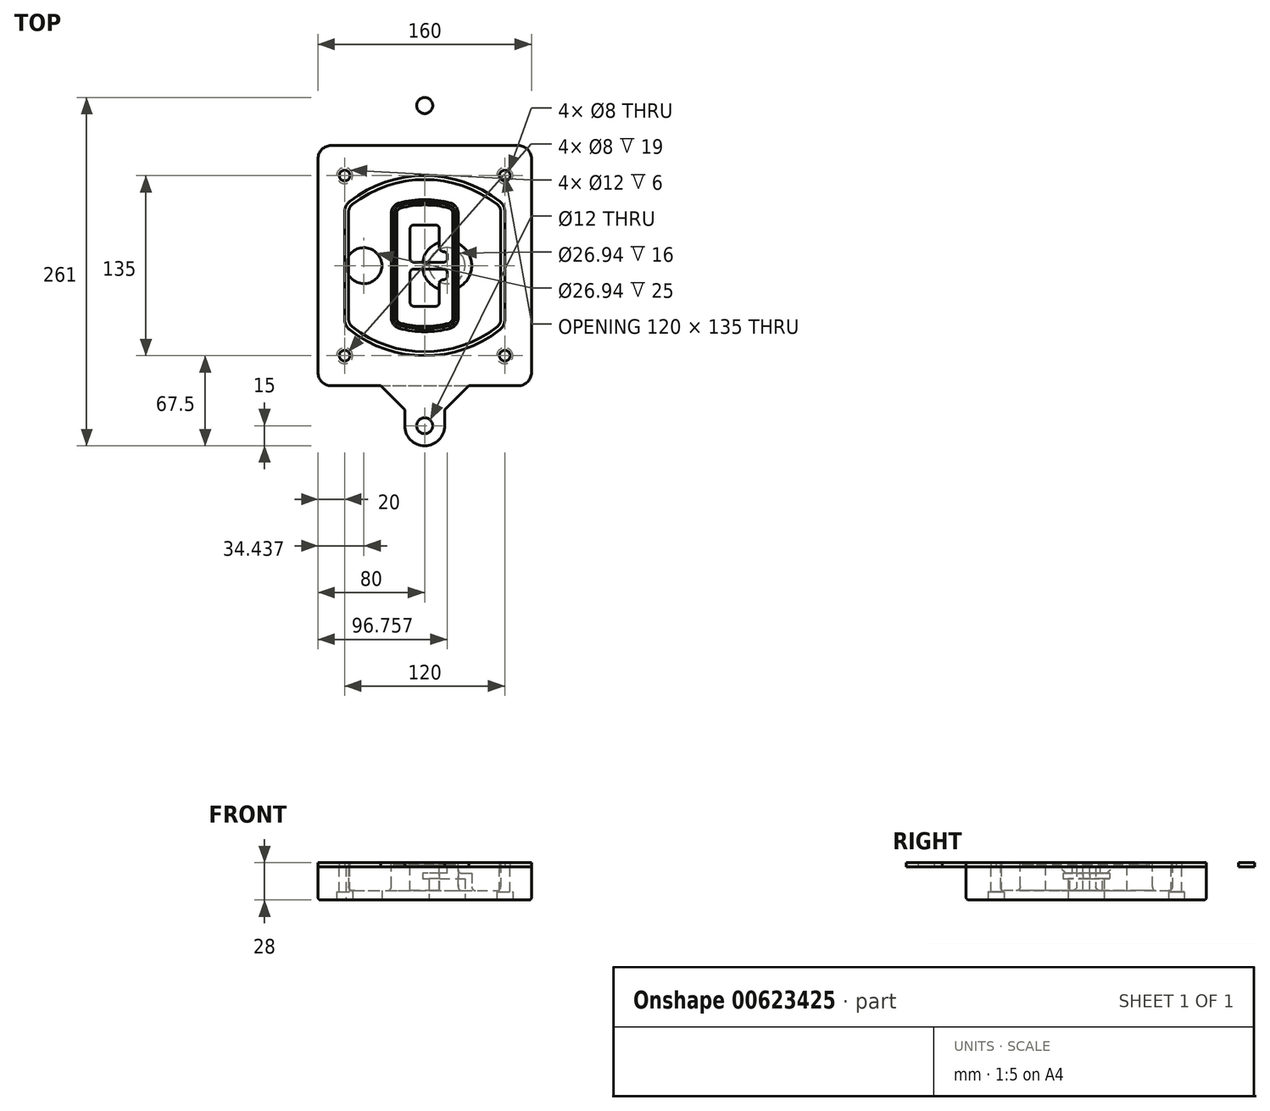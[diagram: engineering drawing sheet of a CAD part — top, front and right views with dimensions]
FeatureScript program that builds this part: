
annotation { "Feature Type Name" : "Feature", "Feature Type Description" : "" }
export const myFeature = defineFeature(function(context is Context, id is Id, definition is map)
    precondition{}
    {
        {
            var Q0;
            Q0=qCreatedBy(makeId("Top.planeOp"),FACE);
            var sketch = newSketch(context, id + "F0", { "sketchPlane" : qUnion([Q0])});
            skPoint(sketch, "E0.rect.middle", {"position": v(0, 0) * mm});
            skLineSegment(sketch, "E1.bottom", {"start": v(-70, -90) * mm, "end": v(70, -90) * mm});
            skLineSegment(sketch, "E1.top", {"start": v(-70, 90) * mm, "end": v(70, 90) * mm});
            skLineSegment(sketch, "E1.left", {"start": v(-80, -80) * mm, "end": v(-80, 80) * mm});
            skLineSegment(sketch, "E1.right", {"start": v(80, -80) * mm, "end": v(80, 80) * mm});
            skLineSegment(sketch, "E2", {"start": v(-80, 90) * mm, "end": v(80, -90) * mm, "construction": true});
            skLineSegment(sketch, "E3", {"start": v(80, 90) * mm, "end": v(-80, -90) * mm, "construction": true});
            skCircle(sketch, "E4", {"center": v(-60, 67.5) * mm, "radius": 4 * mm});
            skCircle(sketch, "E5", {"center": v(60, 67.5) * mm, "radius": 4 * mm});
            skCircle(sketch, "E6", {"center": v(60, -67.5) * mm, "radius": 4 * mm});
            skCircle(sketch, "E7", {"center": v(-60, -67.5) * mm, "radius": 4 * mm});
            skLineSegment(sketch, "E8", {"start": v(-60, 67.5) * mm, "end": v(60, 67.5) * mm, "construction": true});
            skLineSegment(sketch, "E9", {"start": v(60, 67.5) * mm, "end": v(60, -67.5) * mm, "construction": true});
            skLineSegment(sketch, "E10", {"start": v(60, -67.5) * mm, "end": v(-60, -67.5) * mm, "construction": true});
            skLineSegment(sketch, "E11", {"start": v(-60, -67.5) * mm, "end": v(-60, 67.5) * mm, "construction": true});
            skLineSegment(sketch, "E12", {"start": v(-60, 40.3) * mm, "end": v(-60, -40.3) * mm});
            skLineSegment(sketch, "E13", {"start": v(60, 40.3) * mm, "end": v(60, -40.3) * mm});
            skArc(sketch, "E14", {"start": v(56.15, 48.18) * mm, "mid": v(0, 67.5) * mm, "end": v(-56.15, 48.18) * mm});
            skArc(sketch, "E15", {"start": v(-56.15, -48.18) * mm, "mid": v(0, -67.5) * mm, "end": v(56.15, -48.18) * mm});
            skLineSegment(sketch, "E16", {"start": v(-60, 0) * mm, "end": v(60, 0) * mm, "construction": true});
            skPoint(sketch, "E17.visualSharp", {"position": v(-60, -45) * mm});
            skArc(sketch, "E17.filletArc", {"start": v(-60, -40.3) * mm, "mid": v(-58.99, -44.68) * mm, "end": v(-56.15, -48.18) * mm});
            skPoint(sketch, "E18.visualSharp", {"position": v(-60, 45) * mm});
            skArc(sketch, "E18.filletArc", {"start": v(-56.15, 48.18) * mm, "mid": v(-58.99, 44.68) * mm, "end": v(-60, 40.3) * mm});
            skPoint(sketch, "E19.visualSharp", {"position": v(60, 45) * mm});
            skArc(sketch, "E19.filletArc", {"start": v(60, 40.3) * mm, "mid": v(58.99, 44.68) * mm, "end": v(56.15, 48.18) * mm});
            skPoint(sketch, "E20.visualSharp", {"position": v(60, -45) * mm});
            skArc(sketch, "E20.filletArc", {"start": v(56.15, -48.18) * mm, "mid": v(58.99, -44.68) * mm, "end": v(60, -40.3) * mm});
            skPoint(sketch, "E21.visualSharp", {"position": v(-80, 90) * mm});
            skArc(sketch, "E21.filletArc", {"start": v(-70, 90) * mm, "mid": v(-77.07, 87.07) * mm, "end": v(-80, 80) * mm});
            skPoint(sketch, "E22.visualSharp", {"position": v(80, 90) * mm});
            skArc(sketch, "E22.filletArc", {"start": v(80, 80) * mm, "mid": v(77.07, 87.07) * mm, "end": v(70, 90) * mm});
            skPoint(sketch, "E23.visualSharp", {"position": v(80, -90) * mm});
            skArc(sketch, "E23.filletArc", {"start": v(70, -90) * mm, "mid": v(77.07, -87.07) * mm, "end": v(80, -80) * mm});
            skPoint(sketch, "E24.visualSharp", {"position": v(-80, -90) * mm});
            skArc(sketch, "E24.filletArc", {"start": v(-80, -80) * mm, "mid": v(-77.07, -87.07) * mm, "end": v(-70, -90) * mm});
            skArc(sketch, "E25.0", {"start": v(57, 40.3) * mm, "mid": v(56.3, 43.36) * mm, "end": v(54.3, 45.81) * mm});
            skLineSegment(sketch, "E25.1", {"start": v(57, 40.3) * mm, "end": v(57, -40.3) * mm});
            skArc(sketch, "E25.2", {"start": v(54.3, -45.81) * mm, "mid": v(56.3, -43.36) * mm, "end": v(57, -40.3) * mm});
            skArc(sketch, "E25.3", {"start": v(-54.3, -45.81) * mm, "mid": v(0, -64.5) * mm, "end": v(54.3, -45.81) * mm});
            skArc(sketch, "E25.4", {"start": v(-57, -40.3) * mm, "mid": v(-56.3, -43.36) * mm, "end": v(-54.3, -45.81) * mm});
            skArc(sketch, "E25.5", {"start": v(54.3, 45.81) * mm, "mid": v(0, 64.5) * mm, "end": v(-54.3, 45.81) * mm});
            skLineSegment(sketch, "E25.6", {"start": v(-57, 40.3) * mm, "end": v(-57, -40.3) * mm});
            skArc(sketch, "E25.7", {"start": v(-54.3, 45.81) * mm, "mid": v(-56.3, 43.36) * mm, "end": v(-57, 40.3) * mm});
            skArc(sketch, "E26.0", {"start": v(-58.62, 51.33) * mm, "mid": v(-62.58, 46.43) * mm, "end": v(-64, 40.3) * mm});
            skArc(sketch, "E26.1", {"start": v(58.62, 51.33) * mm, "mid": v(0, 71.5) * mm, "end": v(-58.62, 51.33) * mm});
            skArc(sketch, "E26.2", {"start": v(64, 40.3) * mm, "mid": v(62.58, 46.43) * mm, "end": v(58.62, 51.33) * mm});
            skLineSegment(sketch, "E26.3", {"start": v(64, 40.3) * mm, "end": v(64, -40.3) * mm});
            skArc(sketch, "E26.4", {"start": v(58.62, -51.33) * mm, "mid": v(62.58, -46.43) * mm, "end": v(64, -40.3) * mm});
            skLineSegment(sketch, "E26.5", {"start": v(-64, 40.3) * mm, "end": v(-64, -40.3) * mm});
            skArc(sketch, "E26.6", {"start": v(-58.62, -51.33) * mm, "mid": v(0, -71.5) * mm, "end": v(58.62, -51.33) * mm});
            skArc(sketch, "E26.7", {"start": v(-64, -40.3) * mm, "mid": v(-62.58, -46.43) * mm, "end": v(-58.62, -51.33) * mm});
            skSolve(sketch);
        }
        {
            var Q0;
            Q0=makeQuery(id+"F0.imprint","IMPRINT",FACE,{"disambiguationData":[TD([[makeQuery(id+"F0.imprint","IMPRINT",EDGE,{"derivedFrom":sQuery(id+"F0.wireOp",EDGE,"E1.bottom")}),1.0]])]});
            var Q1;
            Q1=makeQuery(id+"F0.imprint","IMPRINT",FACE,{"disambiguationData":[TD([[makeQuery(id+"F0.imprint","IMPRINT",EDGE,{"derivedFrom":sQuery(id+"F0.wireOp",EDGE,"E12")}),1.0]])]});
            var Q2;
            Q2=makeQuery(id+"F0.imprint","IMPRINT",FACE,{"disambiguationData":[TD([[makeQuery(id+"F0.imprint","IMPRINT",EDGE,{"derivedFrom":sQuery(id+"F0.wireOp",EDGE,"E25.0")}),1.0]])]});
            var Q3;
            Q3=makeQuery(id+"F0.imprint","IMPRINT",FACE,{"disambiguationData":[TD([[makeQuery(id+"F0.imprint","IMPRINT",EDGE,{"derivedFrom":sQuery(id+"F0.wireOp",EDGE,"E12")}),-1.0]])]});
            extrude(context, id + "F1", {"entities" : qUnion([Q0, Q1, Q2, Q3]), "oppositeDirection" : true, "depth" : 25 * mm});
        }
        {
            var Q0;
            Q0=makeQuery(id+"F0.imprint","IMPRINT",FACE,{"disambiguationData":[TD([[makeQuery(id+"F0.imprint","IMPRINT",EDGE,{"derivedFrom":sQuery(id+"F0.wireOp",EDGE,"E12")}),1.0]])]});
            extrude(context, id + "F2", {"entities" : qUnion([Q0]), "operationType" : NewBodyOperationType.ADD, "depth" : 3 * mm});
        }
        {
            var Q0;
            Q0=makeQuery(id+"F0.imprint","IMPRINT",FACE,{"disambiguationData":[TD([[makeQuery(id+"F0.imprint","IMPRINT",EDGE,{"derivedFrom":sQuery(id+"F0.wireOp",EDGE,"E25.0")}),1.0]])]});
            extrude(context, id + "F3", {"entities" : qUnion([Q0]), "operationType" : NewBodyOperationType.REMOVE, "oppositeDirection" : true, "depth" : 18 * mm});
        }
        {
            var Q0;
            Q0=makeQuery(id+"F2.opExtrude","CAP_FACE",FACE,{"disambiguationData":[OSD([sQuery(id+"F0.wireOp",EDGE,"E12"),sQuery(id+"F0.wireOp",EDGE,"E13"),sQuery(id+"F0.wireOp",EDGE,"E14"),sQuery(id+"F0.wireOp",EDGE,"E15"),sQuery(id+"F0.wireOp",EDGE,"E17.filletArc"),sQuery(id+"F0.wireOp",EDGE,"E18.filletArc"),sQuery(id+"F0.wireOp",EDGE,"E19.filletArc"),sQuery(id+"F0.wireOp",EDGE,"E20.filletArc"),sQuery(id+"F0.wireOp",EDGE,"E25.0"),sQuery(id+"F0.wireOp",EDGE,"E25.1"),sQuery(id+"F0.wireOp",EDGE,"E25.2"),sQuery(id+"F0.wireOp",EDGE,"E25.3"),sQuery(id+"F0.wireOp",EDGE,"E25.4"),sQuery(id+"F0.wireOp",EDGE,"E25.5"),sQuery(id+"F0.wireOp",EDGE,"E25.6"),sQuery(id+"F0.wireOp",EDGE,"E25.7")])],"isStart":false});
            var sketch = newSketch(context, id + "F4", { "sketchPlane" : qUnion([Q0])});
            skArc(sketch, "E27.0", {"start": v(-19.08, -46.97) * mm, "mid": v(0, -49.5) * mm, "end": v(19.08, -46.97) * mm});
            skArc(sketch, "E28.0", {"start": v(19.08, 46.97) * mm, "mid": v(0, 49.5) * mm, "end": v(-19.08, 46.97) * mm});
            skLineSegment(sketch, "E29", {"start": v(-25, 39.25) * mm, "end": v(-25, -39.25) * mm});
            skLineSegment(sketch, "E30", {"start": v(25, 39.25) * mm, "end": v(25, -39.25) * mm});
            skLineSegment(sketch, "E31", {"start": v(-25, 45.1) * mm, "end": v(25, 45.1) * mm, "construction": true});
            skLineSegment(sketch, "E32", {"start": v(-25, -45.1) * mm, "end": v(25, -45.1) * mm, "construction": true});
            skPoint(sketch, "E33.visualSharp", {"position": v(-25, 45.1) * mm});
            skArc(sketch, "E33.filletArc", {"start": v(-19.08, 46.97) * mm, "mid": v(-23.35, 44.11) * mm, "end": v(-25, 39.25) * mm});
            skPoint(sketch, "E34.visualSharp", {"position": v(25, 45.1) * mm});
            skArc(sketch, "E34.filletArc", {"start": v(25, 39.25) * mm, "mid": v(23.35, 44.11) * mm, "end": v(19.08, 46.97) * mm});
            skPoint(sketch, "E35.visualSharp", {"position": v(25, -45.1) * mm});
            skArc(sketch, "E35.filletArc", {"start": v(19.08, -46.97) * mm, "mid": v(23.35, -44.11) * mm, "end": v(25, -39.25) * mm});
            skPoint(sketch, "E36.visualSharp", {"position": v(-25, -45.1) * mm});
            skArc(sketch, "E36.filletArc", {"start": v(-25, -39.25) * mm, "mid": v(-23.35, -44.11) * mm, "end": v(-19.08, -46.97) * mm});
            skArc(sketch, "E37.0", {"start": v(54.3, 45.81) * mm, "mid": v(0, 64.5) * mm, "end": v(-54.3, 45.81) * mm});
            skArc(sketch, "E37.1", {"start": v(-54.3, 45.81) * mm, "mid": v(-56.3, 43.36) * mm, "end": v(-57, 40.3) * mm});
            skLineSegment(sketch, "E37.2", {"start": v(-57, 40.3) * mm, "end": v(-57, -40.3) * mm});
            skArc(sketch, "E37.3", {"start": v(-57, -40.3) * mm, "mid": v(-56.3, -43.36) * mm, "end": v(-54.3, -45.81) * mm});
            skArc(sketch, "E37.4", {"start": v(-54.3, -45.81) * mm, "mid": v(0, -64.5) * mm, "end": v(54.3, -45.81) * mm});
            skArc(sketch, "E37.5", {"start": v(54.3, -45.81) * mm, "mid": v(56.3, -43.36) * mm, "end": v(57, -40.3) * mm});
            skLineSegment(sketch, "E37.6", {"start": v(57, 40.3) * mm, "end": v(57, -40.3) * mm});
            skArc(sketch, "E37.7", {"start": v(57, 40.3) * mm, "mid": v(56.3, 43.36) * mm, "end": v(54.3, 45.81) * mm});
            skLineSegment(sketch, "E38.0", {"start": v(23, 39.25) * mm, "end": v(23, -39.25) * mm});
            skArc(sketch, "E38.1", {"start": v(18.56, -45.04) * mm, "mid": v(21.76, -42.9) * mm, "end": v(23, -39.25) * mm});
            skArc(sketch, "E38.2", {"start": v(-18.56, -45.04) * mm, "mid": v(0, -47.5) * mm, "end": v(18.56, -45.04) * mm});
            skArc(sketch, "E38.3", {"start": v(-23, -39.25) * mm, "mid": v(-21.76, -42.9) * mm, "end": v(-18.56, -45.04) * mm});
            skLineSegment(sketch, "E38.4", {"start": v(-23, 39.25) * mm, "end": v(-23, -39.25) * mm});
            skArc(sketch, "E38.5", {"start": v(23, 39.25) * mm, "mid": v(21.76, 42.9) * mm, "end": v(18.56, 45.04) * mm});
            skArc(sketch, "E38.6", {"start": v(-18.56, 45.04) * mm, "mid": v(-21.76, 42.9) * mm, "end": v(-23, 39.25) * mm});
            skArc(sketch, "E38.7", {"start": v(18.56, 45.04) * mm, "mid": v(0, 47.5) * mm, "end": v(-18.56, 45.04) * mm});
            skArc(sketch, "E39.0", {"start": v(21, 39.25) * mm, "mid": v(20.18, 41.68) * mm, "end": v(18.04, 43.1) * mm});
            skLineSegment(sketch, "E39.1", {"start": v(21, 39.25) * mm, "end": v(21, -39.25) * mm});
            skArc(sketch, "E39.2", {"start": v(18.04, -43.1) * mm, "mid": v(20.18, -41.68) * mm, "end": v(21, -39.25) * mm});
            skArc(sketch, "E39.3", {"start": v(-18.04, -43.1) * mm, "mid": v(0, -45.5) * mm, "end": v(18.04, -43.1) * mm});
            skArc(sketch, "E39.4", {"start": v(-21, -39.25) * mm, "mid": v(-20.18, -41.68) * mm, "end": v(-18.04, -43.1) * mm});
            skArc(sketch, "E39.5", {"start": v(18.04, 43.1) * mm, "mid": v(0, 45.5) * mm, "end": v(-18.04, 43.1) * mm});
            skLineSegment(sketch, "E39.6", {"start": v(-21, 39.25) * mm, "end": v(-21, -39.25) * mm});
            skArc(sketch, "E39.7", {"start": v(-18.04, 43.1) * mm, "mid": v(-20.18, 41.68) * mm, "end": v(-21, 39.25) * mm});
            skLineSegment(sketch, "E40", {"start": v(-25, 0) * mm, "end": v(25, 0) * mm, "construction": true});
            skLineSegment(sketch, "E41", {"start": v(-11, 5.5) * mm, "end": v(-11, 27.5) * mm});
            skLineSegment(sketch, "E42", {"start": v(-8, 30.5) * mm, "end": v(8, 30.5) * mm});
            skLineSegment(sketch, "E43", {"start": v(11, 27.5) * mm, "end": v(11, 13.5) * mm});
            skLineSegment(sketch, "E44", {"start": v(14, 10.5) * mm, "end": v(14, 10.5) * mm});
            skLineSegment(sketch, "E45", {"start": v(17, 7.5) * mm, "end": v(17, 5.5) * mm});
            skLineSegment(sketch, "E46", {"start": v(14, 2.5) * mm, "end": v(-8, 2.5) * mm});
            skPoint(sketch, "E47.visualSharp", {"position": v(-11, 30.5) * mm});
            skArc(sketch, "E47.filletArc", {"start": v(-8, 30.5) * mm, "mid": v(-10.12, 29.62) * mm, "end": v(-11, 27.5) * mm});
            skPoint(sketch, "E48.visualSharp", {"position": v(11, 30.5) * mm});
            skArc(sketch, "E48.filletArc", {"start": v(11, 27.5) * mm, "mid": v(10.12, 29.62) * mm, "end": v(8, 30.5) * mm});
            skPoint(sketch, "E49.visualSharp", {"position": v(11, 10.5) * mm});
            skArc(sketch, "E49.filletArc", {"start": v(11, 13.5) * mm, "mid": v(11.88, 11.38) * mm, "end": v(14, 10.5) * mm});
            skPoint(sketch, "E50.visualSharp", {"position": v(17, 10.5) * mm});
            skArc(sketch, "E50.filletArc", {"start": v(17, 7.5) * mm, "mid": v(16.12, 9.62) * mm, "end": v(14, 10.5) * mm});
            skPoint(sketch, "E51.visualSharp", {"position": v(17, 2.5) * mm});
            skArc(sketch, "E51.filletArc", {"start": v(14, 2.5) * mm, "mid": v(16.12, 3.38) * mm, "end": v(17, 5.5) * mm});
            skPoint(sketch, "E52.visualSharp", {"position": v(-11, 2.5) * mm});
            skArc(sketch, "E52.filletArc", {"start": v(-11, 5.5) * mm, "mid": v(-10.12, 3.38) * mm, "end": v(-8, 2.5) * mm});
            skLineSegment(sketch, "E53.0.MirrorCS", {"start": v(14, -2.5) * mm, "end": v(-8, -2.5) * mm});
            skArc(sketch, "E54.0.MirrorCS", {"start": v(-11, -5.5) * mm, "mid": v(-10.12, -3.38) * mm, "end": v(-8, -2.5) * mm});
            skLineSegment(sketch, "E55.0.MirrorCS", {"start": v(-11, -5.5) * mm, "end": v(-11, -27.5) * mm});
            skArc(sketch, "E56.0.MirrorCS", {"start": v(-8, -30.5) * mm, "mid": v(-10.12, -29.62) * mm, "end": v(-11, -27.5) * mm});
            skLineSegment(sketch, "E57.0.MirrorCS", {"start": v(-8, -30.5) * mm, "end": v(8, -30.5) * mm});
            skArc(sketch, "E58.0.MirrorCS", {"start": v(11, -27.5) * mm, "mid": v(10.12, -29.62) * mm, "end": v(8, -30.5) * mm});
            skLineSegment(sketch, "E59.0.MirrorCS", {"start": v(11, -27.5) * mm, "end": v(11, -13.5) * mm});
            skArc(sketch, "E60.0.MirrorCS", {"start": v(11, -13.5) * mm, "mid": v(11.88, -11.38) * mm, "end": v(14, -10.5) * mm});
            skArc(sketch, "E61.0.MirrorCS", {"start": v(17, -7.5) * mm, "mid": v(16.12, -9.62) * mm, "end": v(14, -10.5) * mm});
            skLineSegment(sketch, "E62.0.MirrorCS", {"start": v(17, -7.5) * mm, "end": v(17, -5.5) * mm});
            skArc(sketch, "E63.0.MirrorCS", {"start": v(14, -2.5) * mm, "mid": v(16.12, -3.38) * mm, "end": v(17, -5.5) * mm});
            skSolve(sketch);
        }
        {
            var Q0;
            Q0=makeQuery(id+"F4.imprint","IMPRINT",FACE,{"disambiguationData":[TD([[makeQuery(id+"F4.imprint","IMPRINT",EDGE,{"derivedFrom":sQuery(id+"F4.wireOp",EDGE,"E27.0")}),1.0]])]});
            var Q1;
            Q1=makeQuery(id+"F4.imprint","IMPRINT",FACE,{"disambiguationData":[TD([[makeQuery(id+"F4.imprint","IMPRINT",EDGE,{"derivedFrom":sQuery(id+"F4.wireOp",EDGE,"E38.0")}),-1.0]])]});
            var Q2;
            Q2=makeQuery(id+"F4.imprint","IMPRINT",FACE,{"disambiguationData":[TD([[makeQuery(id+"F4.imprint","IMPRINT",EDGE,{"derivedFrom":sQuery(id+"F4.wireOp",EDGE,"E39.0")}),1.0]])]});
            extrude(context, id + "F5", {"entities" : qUnion([Q0, Q1, Q2]), "operationType" : NewBodyOperationType.ADD, "endBound" : BoundingType.UP_TO_NEXT, "oppositeDirection" : true, "depth" : 25 * mm});
        }
        {
            var Q0;
            Q0=makeQuery(id+"F4.imprint","IMPRINT",FACE,{"disambiguationData":[TD([[makeQuery(id+"F4.imprint","IMPRINT",EDGE,{"derivedFrom":sQuery(id+"F4.wireOp",EDGE,"E38.0")}),-1.0]])]});
            extrude(context, id + "F6", {"entities" : qUnion([Q0]), "operationType" : NewBodyOperationType.REMOVE, "oppositeDirection" : true, "depth" : 2 * mm});
        }
        {
            var Q0;
            Q0=makeQuery(id+"F1.opExtrude","CAP_FACE",FACE,{"disambiguationData":[OSD([sQuery(id+"F0.wireOp",EDGE,"E1.bottom"),sQuery(id+"F0.wireOp",EDGE,"E1.top"),sQuery(id+"F0.wireOp",EDGE,"E1.left"),sQuery(id+"F0.wireOp",EDGE,"E1.right"),sQuery(id+"F0.wireOp",EDGE,"E4"),sQuery(id+"F0.wireOp",EDGE,"E5"),sQuery(id+"F0.wireOp",EDGE,"E6"),sQuery(id+"F0.wireOp",EDGE,"E7"),sQuery(id+"F0.wireOp",EDGE,"E21.filletArc"),sQuery(id+"F0.wireOp",EDGE,"E22.filletArc"),sQuery(id+"F0.wireOp",EDGE,"E23.filletArc"),sQuery(id+"F0.wireOp",EDGE,"E24.filletArc")])],"isStart":false});
            var sketch = newSketch(context, id + "F7", { "sketchPlane" : qUnion([Q0])});
            skCircle(sketch, "E64", {"center": v(16.76, 0) * mm, "radius": 13.47 * mm});
            skCircle(sketch, "E65", {"center": v(-45.56, 0) * mm, "radius": 13.47 * mm});
            skLineSegment(sketch, "E66", {"start": v(80, 0) * mm, "end": v(-80, 0) * mm});
            skCircle(sketch, "E67", {"center": v(16.76, 0) * mm, "radius": 18.47 * mm});
            skCircle(sketch, "E68", {"center": v(60, -67.5) * mm, "radius": 6 * mm});
            skCircle(sketch, "E69", {"center": v(-60, -67.5) * mm, "radius": 6 * mm});
            skCircle(sketch, "E70", {"center": v(-60, 67.5) * mm, "radius": 6 * mm});
            skCircle(sketch, "E71", {"center": v(60, 67.5) * mm, "radius": 6 * mm});
            skSolve(sketch);
        }
        {
            var Q0;
            {var subQ1=sQuery(id+"F7.wireOp",EDGE,"E66");var subQ4=sQuery(id+"F7.wireOp",EDGE,"E64");var subQ6=makeQuery(id+"F7.imprint","INTERSECT",VERTEX,{"disambiguationData":[OD(0.0)],"derivedFrom":[subQ4,subQ1]});Q0=makeQuery(id+"F7.imprint","IMPRINT",FACE,{"disambiguationData":[TD([[makeQuery(id+"F7.imprint","IMPRINT",EDGE,{"disambiguationData":[TD([[subQ6,-1.0]])],"derivedFrom":subQ4}),-1.0]])]});}
            var Q1;
            {var subQ0=sQuery(id+"F7.wireOp",EDGE,"E66");var subQ1=sQuery(id+"F7.wireOp",EDGE,"E64");var subQ3=makeQuery(id+"F7.imprint","INTERSECT",VERTEX,{"disambiguationData":[OD(0.0)],"derivedFrom":[subQ1,subQ0]});Q1=makeQuery(id+"F7.imprint","IMPRINT",FACE,{"disambiguationData":[TD([[makeQuery(id+"F7.imprint","IMPRINT",EDGE,{"disambiguationData":[TD([[subQ3,-1.0]])],"derivedFrom":subQ1}),1.0]])]});}
            var Q2;
            {var subQ0=sQuery(id+"F7.wireOp",EDGE,"E66");var subQ1=sQuery(id+"F7.wireOp",EDGE,"E64");var subQ3=makeQuery(id+"F7.imprint","INTERSECT",VERTEX,{"disambiguationData":[OD(0.0)],"derivedFrom":[subQ1,subQ0]});Q2=makeQuery(id+"F7.imprint","IMPRINT",FACE,{"disambiguationData":[TD([[makeQuery(id+"F7.imprint","IMPRINT",EDGE,{"disambiguationData":[TD([[subQ3,1.0]])],"derivedFrom":subQ1}),1.0]])]});}
            var Q3;
            {var subQ1=sQuery(id+"F7.wireOp",EDGE,"E66");var subQ4=sQuery(id+"F7.wireOp",EDGE,"E64");var subQ6=makeQuery(id+"F7.imprint","INTERSECT",VERTEX,{"disambiguationData":[OD(0.0)],"derivedFrom":[subQ4,subQ1]});Q3=makeQuery(id+"F7.imprint","IMPRINT",FACE,{"disambiguationData":[TD([[makeQuery(id+"F7.imprint","IMPRINT",EDGE,{"disambiguationData":[TD([[subQ6,1.0]])],"derivedFrom":subQ4}),-1.0]])]});}
            extrude(context, id + "F8", {"entities" : qUnion([Q0, Q1, Q2, Q3]), "operationType" : NewBodyOperationType.ADD, "oppositeDirection" : true, "depth" : 20 * mm});
        }
        {
            var Q0;
            {var subQ0=sQuery(id+"F7.wireOp",EDGE,"E66");var subQ1=sQuery(id+"F7.wireOp",EDGE,"E64");var subQ3=makeQuery(id+"F7.imprint","INTERSECT",VERTEX,{"disambiguationData":[OD(0.0)],"derivedFrom":[subQ1,subQ0]});Q0=makeQuery(id+"F7.imprint","IMPRINT",FACE,{"disambiguationData":[TD([[makeQuery(id+"F7.imprint","IMPRINT",EDGE,{"disambiguationData":[TD([[subQ3,-1.0]])],"derivedFrom":subQ1}),1.0]])]});}
            var Q1;
            {var subQ0=sQuery(id+"F7.wireOp",EDGE,"E66");var subQ1=sQuery(id+"F7.wireOp",EDGE,"E64");var subQ3=makeQuery(id+"F7.imprint","INTERSECT",VERTEX,{"disambiguationData":[OD(0.0)],"derivedFrom":[subQ1,subQ0]});Q1=makeQuery(id+"F7.imprint","IMPRINT",FACE,{"disambiguationData":[TD([[makeQuery(id+"F7.imprint","IMPRINT",EDGE,{"disambiguationData":[TD([[subQ3,1.0]])],"derivedFrom":subQ1}),1.0]])]});}
            extrude(context, id + "F9", {"entities" : qUnion([Q0, Q1]), "operationType" : NewBodyOperationType.REMOVE, "oppositeDirection" : true, "depth" : 16 * mm});
        }
        {
            var Q0;
            {var subQ0=sQuery(id+"F7.wireOp",EDGE,"E66");var subQ1=sQuery(id+"F7.wireOp",EDGE,"E65");var subQ3=makeQuery(id+"F7.imprint","INTERSECT",VERTEX,{"disambiguationData":[OD(0.0)],"derivedFrom":[subQ1,subQ0]});Q0=makeQuery(id+"F7.imprint","IMPRINT",FACE,{"disambiguationData":[TD([[makeQuery(id+"F7.imprint","IMPRINT",EDGE,{"disambiguationData":[TD([[subQ3,-1.0]])],"derivedFrom":subQ1}),1.0]])]});}
            var Q1;
            {var subQ0=sQuery(id+"F7.wireOp",EDGE,"E66");var subQ1=sQuery(id+"F7.wireOp",EDGE,"E65");var subQ3=makeQuery(id+"F7.imprint","INTERSECT",VERTEX,{"disambiguationData":[OD(0.0)],"derivedFrom":[subQ1,subQ0]});Q1=makeQuery(id+"F7.imprint","IMPRINT",FACE,{"disambiguationData":[TD([[makeQuery(id+"F7.imprint","IMPRINT",EDGE,{"disambiguationData":[TD([[subQ3,1.0]])],"derivedFrom":subQ1}),1.0]])]});}
            extrude(context, id + "F10", {"entities" : qUnion([Q0, Q1]), "operationType" : NewBodyOperationType.REMOVE, "oppositeDirection" : true, "depth" : 25 * mm});
        }
        {
            var Q0;
            Q0=makeQuery(id+"F7.imprint","IMPRINT",FACE,{"disambiguationData":[TD([[makeQuery(id+"F7.imprint","IMPRINT",EDGE,{"derivedFrom":sQuery(id+"F7.wireOp",EDGE,"E68")}),1.0]])]});
            var Q1;
            Q1=makeQuery(id+"F7.imprint","IMPRINT",FACE,{"disambiguationData":[TD([[makeQuery(id+"F7.imprint","IMPRINT",EDGE,{"derivedFrom":makeQuery(id+"F1.opExtrude","CAP_EDGE",EDGE,{"disambiguationData":[OSD([sQuery(id+"F0.wireOp",EDGE,"E5")])],"isStart":false})}),-1.0]])]});
            var Q2;
            Q2=makeQuery(id+"F7.imprint","IMPRINT",FACE,{"disambiguationData":[TD([[makeQuery(id+"F7.imprint","IMPRINT",EDGE,{"derivedFrom":sQuery(id+"F7.wireOp",EDGE,"E69")}),1.0]])]});
            var Q3;
            Q3=makeQuery(id+"F7.imprint","IMPRINT",FACE,{"disambiguationData":[TD([[makeQuery(id+"F7.imprint","IMPRINT",EDGE,{"derivedFrom":makeQuery(id+"F1.opExtrude","CAP_EDGE",EDGE,{"disambiguationData":[OSD([sQuery(id+"F0.wireOp",EDGE,"E4")])],"isStart":false})}),-1.0]])]});
            var Q4;
            Q4=makeQuery(id+"F7.imprint","IMPRINT",FACE,{"disambiguationData":[TD([[makeQuery(id+"F7.imprint","IMPRINT",EDGE,{"derivedFrom":sQuery(id+"F7.wireOp",EDGE,"E70")}),1.0]])]});
            var Q5;
            Q5=makeQuery(id+"F7.imprint","IMPRINT",FACE,{"disambiguationData":[TD([[makeQuery(id+"F7.imprint","IMPRINT",EDGE,{"derivedFrom":makeQuery(id+"F1.opExtrude","CAP_EDGE",EDGE,{"disambiguationData":[OSD([sQuery(id+"F0.wireOp",EDGE,"E7")])],"isStart":false})}),-1.0]])]});
            var Q6;
            Q6=makeQuery(id+"F7.imprint","IMPRINT",FACE,{"disambiguationData":[TD([[makeQuery(id+"F7.imprint","IMPRINT",EDGE,{"derivedFrom":sQuery(id+"F7.wireOp",EDGE,"E71")}),1.0]])]});
            var Q7;
            Q7=makeQuery(id+"F7.imprint","IMPRINT",FACE,{"disambiguationData":[TD([[makeQuery(id+"F7.imprint","IMPRINT",EDGE,{"derivedFrom":makeQuery(id+"F1.opExtrude","CAP_EDGE",EDGE,{"disambiguationData":[OSD([sQuery(id+"F0.wireOp",EDGE,"E6")])],"isStart":false})}),-1.0]])]});
            extrude(context, id + "F11", {"entities" : qUnion([Q0, Q1, Q2, Q3, Q4, Q5, Q6, Q7]), "operationType" : NewBodyOperationType.REMOVE, "oppositeDirection" : true, "depth" : 6 * mm});
        }
        {
            var Q0;
            Q0=makeQuery(id+"F9.boolean.opBoolean","COPY",FACE,{"derivedFrom":makeQuery(id+"F9.opExtrude","CAP_FACE",FACE,{"disambiguationData":[OSD([sQuery(id+"F7.wireOp",EDGE,"E64")])],"isStart":false})});
            var sketch = newSketch(context, id + "F12", { "sketchPlane" : qUnion([Q0])});
            skArc(sketch, "E72.0", {"start": v(11, 17.55) * mm, "mid": v(2.57, 11.82) * mm, "end": v(-1.54, 2.5) * mm});
            skArc(sketch, "E72.1", {"start": v(-1.54, -2.5) * mm, "mid": v(2.57, -11.82) * mm, "end": v(11, -17.55) * mm});
            skLineSegment(sketch, "E73", {"start": v(-1.54, -2.5) * mm, "end": v(14, -2.5) * mm});
            skLineSegment(sketch, "E74.0", {"start": v(14, 2.5) * mm, "end": v(-1.54, 2.5) * mm});
            skArc(sketch, "E74.1", {"start": v(14, 2.5) * mm, "mid": v(16.12, 3.38) * mm, "end": v(17, 5.5) * mm});
            skLineSegment(sketch, "E74.2", {"start": v(17, 7.5) * mm, "end": v(17, 5.5) * mm});
            skArc(sketch, "E74.3", {"start": v(17, 7.5) * mm, "mid": v(16.12, 9.62) * mm, "end": v(14, 10.5) * mm});
            skArc(sketch, "E74.4", {"start": v(11, 13.5) * mm, "mid": v(11.88, 11.38) * mm, "end": v(14, 10.5) * mm});
            skLineSegment(sketch, "E74.5", {"start": v(11, 17.55) * mm, "end": v(11, 13.5) * mm});
            skLineSegment(sketch, "E74.7", {"start": v(14, -2.5) * mm, "end": v(-1.54, -2.5) * mm});
            skArc(sketch, "E74.8", {"start": v(14, -2.5) * mm, "mid": v(16.12, -3.38) * mm, "end": v(17, -5.5) * mm});
            skLineSegment(sketch, "E74.9", {"start": v(17, -7.5) * mm, "end": v(17, -5.5) * mm});
            skArc(sketch, "E74.10", {"start": v(17, -7.5) * mm, "mid": v(16.12, -9.62) * mm, "end": v(14, -10.5) * mm});
            skArc(sketch, "E74.11", {"start": v(11, -13.5) * mm, "mid": v(11.88, -11.38) * mm, "end": v(14, -10.5) * mm});
            skLineSegment(sketch, "E74.12", {"start": v(11, -17.55) * mm, "end": v(11, -13.5) * mm});
            skPoint(sketch, "E75.orphan", {"position": v(11, -27.5) * mm});
            skPoint(sketch, "E76.orphan", {"position": v(-8, -2.5) * mm});
            skPoint(sketch, "E77.orphan", {"position": v(-8, 2.5) * mm});
            skPoint(sketch, "E78.orphan", {"position": v(11, 27.5) * mm});
            skSolve(sketch);
        }
        {
            var Q0;
            {var subQ7=sQuery(id+"F12.wireOp",EDGE,"E72.0");var subQ14=sQuery(id+"F12.wireOp",EDGE,"E72.1");var subQ16=sQuery(id+"F12.wireOp",EDGE,"E74.1");var subQ18=sQuery(id+"F12.wireOp",EDGE,"E74.8");Q0=qUnion([makeQuery(id+"F12.imprint","IMPRINT",FACE,{"disambiguationData":[TD([[makeQuery(id+"F12.imprint","IMPRINT",EDGE,{"derivedFrom":subQ7}),1.0]])]}),makeQuery(id+"F12.imprint","IMPRINT",FACE,{"disambiguationData":[TD([[makeQuery(id+"F12.imprint","IMPRINT",EDGE,{"derivedFrom":subQ14}),1.0]])]}),makeQuery(id+"F12.imprint","IMPRINT",FACE,{"disambiguationData":[TD([[makeQuery(id+"F12.imprint","IMPRINT",EDGE,{"derivedFrom":subQ16}),1.0]])]}),makeQuery(id+"F12.imprint","IMPRINT",FACE,{"disambiguationData":[TD([[makeQuery(id+"F12.imprint","IMPRINT",EDGE,{"derivedFrom":subQ18}),-1.0]])]})]);}
            var Q1;
            Q1=makeQuery(id+"F5.boolean.opBoolean","SPLIT",FACE,{"disambiguationData":[TD([makeQuery(id+"F5.opExtrude","SWEPT_FACE",FACE,{"disambiguationData":[OSD([sQuery(id+"F4.wireOp",EDGE,"E41")])]})])],"derivedFrom":makeQuery(id+"F3.boolean.opBoolean","COPY",FACE,{"derivedFrom":makeQuery(id+"F3.opExtrude","CAP_FACE",FACE,{"disambiguationData":[OSD([sQuery(id+"F0.wireOp",EDGE,"E25.0"),sQuery(id+"F0.wireOp",EDGE,"E25.1"),sQuery(id+"F0.wireOp",EDGE,"E25.2"),sQuery(id+"F0.wireOp",EDGE,"E25.3"),sQuery(id+"F0.wireOp",EDGE,"E25.4"),sQuery(id+"F0.wireOp",EDGE,"E25.5"),sQuery(id+"F0.wireOp",EDGE,"E25.6"),sQuery(id+"F0.wireOp",EDGE,"E25.7")])],"isStart":false})})});
            extrude(context, id + "F13", {"entities" : qUnion([Q0]), "operationType" : NewBodyOperationType.REMOVE, "endBound" : BoundingType.UP_TO_SURFACE, "endBoundEntityFace" : qUnion([Q1]), "depth" : 25 * mm});
        }
        {
            var Q0;
            Q0=makeQuery(id+"F3.boolean.opBoolean","COPY",EDGE,{"derivedFrom":makeQuery(id+"F3.opExtrude","CAP_EDGE",EDGE,{"disambiguationData":[OSD([sQuery(id+"F0.wireOp",EDGE,"E25.6")])],"isStart":false})});
            var Q1;
            Q1=makeQuery(id+"F8.boolean.opBoolean","INTERSECT",EDGE,{"derivedFrom":[makeQuery(id+"F5.opExtrude","SWEPT_FACE",FACE,{"disambiguationData":[OSD([sQuery(id+"F4.wireOp",EDGE,"E30")])]}),makeQuery(id+"F8.opExtrude","CAP_FACE",FACE,{"disambiguationData":[OSD([sQuery(id+"F7.wireOp",EDGE,"E67")])],"isStart":false})]});
            var Q2;
            Q2=makeQuery(id+"F8.boolean.opBoolean","INTERSECT",EDGE,{"disambiguationData":[OD(1.0)],"derivedFrom":[makeQuery(id+"F5.opExtrude","SWEPT_FACE",FACE,{"disambiguationData":[OSD([sQuery(id+"F4.wireOp",EDGE,"E30")])]}),makeQuery(id+"F8.opExtrude","SWEPT_FACE",FACE,{"disambiguationData":[OSD([sQuery(id+"F7.wireOp",EDGE,"E67")])]})]});
            var Q3;
            {var subQ0=sQuery(id+"F4.wireOp",EDGE,"E30");Q3=makeQuery(id+"F8.boolean.opBoolean","SPLIT",EDGE,{"disambiguationData":[TD([makeQuery(id+"F5.opExtrude","SWEPT_FACE",FACE,{"disambiguationData":[OSD([sQuery(id+"F4.wireOp",EDGE,"E35.filletArc")])]})])],"derivedFrom":makeQuery(id+"F5.opExtrude","CAP_EDGE",EDGE,{"disambiguationData":[OSD([subQ0])],"isStart":false})});}
            var Q4;
            {var subQ0=sQuery(id+"F0.wireOp",EDGE,"E25.7");var subQ1=sQuery(id+"F0.wireOp",EDGE,"E25.1");var subQ2=sQuery(id+"F0.wireOp",EDGE,"E25.6");var subQ3=sQuery(id+"F0.wireOp",EDGE,"E25.5");var subQ4=sQuery(id+"F0.wireOp",EDGE,"E25.4");var subQ5=sQuery(id+"F0.wireOp",EDGE,"E25.0");var subQ6=sQuery(id+"F0.wireOp",EDGE,"E25.2");var subQ7=sQuery(id+"F0.wireOp",EDGE,"E25.3");Q4=makeQuery(id+"F8.boolean.opBoolean","INTERSECT",EDGE,{"derivedFrom":[makeQuery(id+"F5.boolean.opBoolean","SPLIT",FACE,{"disambiguationData":[TD([makeQuery(id+"F2.opExtrude","SWEPT_FACE",FACE,{"disambiguationData":[OSD([subQ5])]})])],"derivedFrom":makeQuery(id+"F3.boolean.opBoolean","COPY",FACE,{"derivedFrom":makeQuery(id+"F3.opExtrude","CAP_FACE",FACE,{"disambiguationData":[OSD([subQ5,subQ1,subQ6,subQ7,subQ4,subQ3,subQ2,subQ0])],"isStart":false})})}),makeQuery(id+"F8.opExtrude","SWEPT_FACE",FACE,{"disambiguationData":[OSD([sQuery(id+"F7.wireOp",EDGE,"E67")])]})]});}
            var Q5;
            Q5=makeQuery(id+"F8.boolean.opBoolean","INTERSECT",EDGE,{"disambiguationData":[OD(0.0)],"derivedFrom":[makeQuery(id+"F5.opExtrude","SWEPT_FACE",FACE,{"disambiguationData":[OSD([sQuery(id+"F4.wireOp",EDGE,"E30")])]}),makeQuery(id+"F8.opExtrude","SWEPT_FACE",FACE,{"disambiguationData":[OSD([sQuery(id+"F7.wireOp",EDGE,"E67")])]})]});
            fillet(context, id + "F14", {"entities" : qUnion([Q0, Q1, Q2, Q3, Q4, Q5]), "radius" : 3 * mm, "tangentPropagation" : true, "allowEdgeOverflow" : false});
        }
        {
            var Q0;
            Q0=makeQuery(id+"F1.opExtrude","CAP_EDGE",EDGE,{"disambiguationData":[OSD([sQuery(id+"F0.wireOp",EDGE,"E1.bottom")])],"isStart":false});
            fillet(context, id + "F15", {"entities" : qUnion([Q0]), "radius" : 2 * mm, "tangentPropagation" : true, "allowEdgeOverflow" : false});
        }
        {
            var Q0;
            {var subQ0=sQuery(id+"F0.wireOp",EDGE,"E21.filletArc");var subQ1=sQuery(id+"F0.wireOp",EDGE,"E7");var subQ2=sQuery(id+"F0.wireOp",EDGE,"E6");var subQ3=sQuery(id+"F0.wireOp",EDGE,"E5");var subQ4=sQuery(id+"F0.wireOp",EDGE,"E4");var subQ5=sQuery(id+"F0.wireOp",EDGE,"E22.filletArc");var subQ6=sQuery(id+"F0.wireOp",EDGE,"E1.bottom");var subQ7=sQuery(id+"F0.wireOp",EDGE,"E1.right");var subQ8=sQuery(id+"F0.wireOp",EDGE,"E1.top");var subQ9=sQuery(id+"F0.wireOp",EDGE,"E1.left");var subQ10=sQuery(id+"F0.wireOp",EDGE,"E23.filletArc");var subQ11=sQuery(id+"F0.wireOp",EDGE,"E24.filletArc");Q0=makeQuery(id+"F2.boolean.opBoolean","SPLIT",FACE,{"disambiguationData":[TD([makeQuery(id+"F1.opExtrude","SWEPT_FACE",FACE,{"disambiguationData":[OSD([subQ6])]})])],"derivedFrom":makeQuery(id+"F1.opExtrude","CAP_FACE",FACE,{"disambiguationData":[OSD([subQ6,subQ8,subQ9,subQ7,subQ4,subQ3,subQ2,subQ1,subQ0,subQ5,subQ10,subQ11])],"isStart":true})});}
            var sketch = newSketch(context, id + "F16", { "sketchPlane" : qUnion([Q0])});
            skLineSegment(sketch, "E79.0", {"start": v(-70, 90) * mm, "end": v(70, 90) * mm});
            skArc(sketch, "E79.1", {"start": v(-70, 90) * mm, "mid": v(-77.07, 87.07) * mm, "end": v(-80, 80) * mm});
            skArc(sketch, "E79.3", {"start": v(-80, -80) * mm, "mid": v(-77.07, -87.07) * mm, "end": v(-70, -90) * mm});
            skLineSegment(sketch, "E79.4", {"start": v(-70, -90) * mm, "end": v(70, -90) * mm});
            skArc(sketch, "E79.5", {"start": v(70, -90) * mm, "mid": v(77.07, -87.07) * mm, "end": v(80, -80) * mm});
            skLineSegment(sketch, "E79.6", {"start": v(80, -80) * mm, "end": v(80, 80) * mm});
            skArc(sketch, "E79.7", {"start": v(80, 80) * mm, "mid": v(77.07, 87.07) * mm, "end": v(70, 90) * mm});
            skCircle(sketch, "E79.8", {"center": v(-60, 67.5) * mm, "radius": 4 * mm});
            skCircle(sketch, "E79.9", {"center": v(-60, -67.5) * mm, "radius": 4 * mm});
            skCircle(sketch, "E79.10", {"center": v(60, 67.5) * mm, "radius": 4 * mm});
            skCircle(sketch, "E79.11", {"center": v(60, -67.5) * mm, "radius": 4 * mm});
            skArc(sketch, "E79.12", {"start": v(56.15, 48.18) * mm, "mid": v(0, 67.5) * mm, "end": v(-56.15, 48.18) * mm});
            skArc(sketch, "E79.13", {"start": v(-56.15, 48.18) * mm, "mid": v(-58.99, 44.68) * mm, "end": v(-60, 40.3) * mm});
            skLineSegment(sketch, "E79.14", {"start": v(-60, 40.3) * mm, "end": v(-60, -40.3) * mm});
            skArc(sketch, "E79.15", {"start": v(-60, -40.3) * mm, "mid": v(-58.99, -44.68) * mm, "end": v(-56.15, -48.18) * mm});
            skArc(sketch, "E79.16", {"start": v(-56.15, -48.18) * mm, "mid": v(0, -67.5) * mm, "end": v(56.15, -48.18) * mm});
            skArc(sketch, "E79.17", {"start": v(56.15, -48.18) * mm, "mid": v(58.99, -44.68) * mm, "end": v(60, -40.3) * mm});
            skLineSegment(sketch, "E79.18", {"start": v(60, 40.3) * mm, "end": v(60, -40.3) * mm});
            skArc(sketch, "E79.19", {"start": v(60, 40.3) * mm, "mid": v(58.99, 44.68) * mm, "end": v(56.15, 48.18) * mm});
            skLineSegment(sketch, "E80", {"start": v(0, 90) * mm, "end": v(0, 120) * mm, "construction": true});
            skPoint(sketch, "E80.endSnap0", {"position": v(0, 90) * mm});
            skCircle(sketch, "E81", {"center": v(0, 120) * mm, "radius": 6 * mm});
            skArc(sketch, "E82", {"start": v(15, 120) * mm, "mid": v(0, 135) * mm, "end": v(-15, 120) * mm});
            skLineSegment(sketch, "E83", {"start": v(-15, 120) * mm, "end": v(-15, 108) * mm});
            skLineSegment(sketch, "E84", {"start": v(-15, 108) * mm, "end": v(-33, 90) * mm});
            skLineSegment(sketch, "E85.MirrorCS", {"start": v(15, 120) * mm, "end": v(15, 108) * mm});
            skLineSegment(sketch, "E86.MirrorCS", {"start": v(15, 108) * mm, "end": v(33, 90) * mm});
            skLineSegment(sketch, "E87", {"start": v(-80, 0) * mm, "end": v(80, 0) * mm, "construction": true});
            skArc(sketch, "E88.MirrorCS", {"start": v(-15, 120) * mm, "mid": v(0, 135) * mm, "end": v(15, 120) * mm});
            skLineSegment(sketch, "E89.MirrorCS", {"start": v(80, 0) * mm, "end": v(-80, 0) * mm, "construction": true});
            skLineSegment(sketch, "E90.MirrorCS", {"start": v(-15, -120) * mm, "end": v(-15, -108) * mm});
            skCircle(sketch, "E91.MirrorC", {"center": v(0, -120) * mm, "radius": 6 * mm});
            skLineSegment(sketch, "E92.MirrorCS", {"start": v(-15, -108) * mm, "end": v(-33, -90) * mm});
            skLineSegment(sketch, "E93.MirrorCS", {"start": v(15, -120) * mm, "end": v(15, -108) * mm});
            skArc(sketch, "E94.MirrorCS", {"start": v(15, -120) * mm, "mid": v(0, -135) * mm, "end": v(-15, -120) * mm});
            skLineSegment(sketch, "E95.MirrorCS", {"start": v(15, -108) * mm, "end": v(33, -90) * mm});
            skPoint(sketch, "E96.MirrorP", {"position": v(0, -90) * mm});
            skArc(sketch, "E97.MirrorCS", {"start": v(-15, -120) * mm, "mid": v(0, -135) * mm, "end": v(15, -120) * mm});
            skLineSegment(sketch, "E98.MirrorCS", {"start": v(0, -90) * mm, "end": v(0, -120) * mm, "construction": true});
            skSolve(sketch);
        }
        {
            var Q0;
            Q0=makeQuery(id+"F16.imprint","IMPRINT",FACE,{"disambiguationData":[TD([[makeQuery(id+"F16.imprint","IMPRINT",EDGE,{"derivedFrom":sQuery(id+"F16.wireOp",EDGE,"E81")}),1.0]])]});
            var Q1;
            {var subQ1=sQuery(id+"F16.wireOp",EDGE,"E79.1");Q1=makeQuery(id+"F16.imprint","IMPRINT",FACE,{"disambiguationData":[TD([[makeQuery(id+"F16.imprint","IMPRINT",EDGE,{"derivedFrom":subQ1}),1.0]])]});}
            var Q2;
            {var subQ0=sQuery(id+"F16.wireOp",EDGE,"E92.MirrorCS");Q2=makeQuery(id+"F16.imprint","IMPRINT",FACE,{"disambiguationData":[TD([[makeQuery(id+"F16.imprint","IMPRINT",EDGE,{"derivedFrom":subQ0}),-1.0]])]});}
            var Q3;
            Q3=makeQuery(id+"F2.opExtrude","CAP_FACE",FACE,{"disambiguationData":[OSD([sQuery(id+"F0.wireOp",EDGE,"E12"),sQuery(id+"F0.wireOp",EDGE,"E13"),sQuery(id+"F0.wireOp",EDGE,"E14"),sQuery(id+"F0.wireOp",EDGE,"E15"),sQuery(id+"F0.wireOp",EDGE,"E17.filletArc"),sQuery(id+"F0.wireOp",EDGE,"E18.filletArc"),sQuery(id+"F0.wireOp",EDGE,"E19.filletArc"),sQuery(id+"F0.wireOp",EDGE,"E20.filletArc"),sQuery(id+"F0.wireOp",EDGE,"E25.0"),sQuery(id+"F0.wireOp",EDGE,"E25.1"),sQuery(id+"F0.wireOp",EDGE,"E25.2"),sQuery(id+"F0.wireOp",EDGE,"E25.3"),sQuery(id+"F0.wireOp",EDGE,"E25.4"),sQuery(id+"F0.wireOp",EDGE,"E25.5"),sQuery(id+"F0.wireOp",EDGE,"E25.6"),sQuery(id+"F0.wireOp",EDGE,"E25.7")])],"isStart":false});
            extrude(context, id + "F17", {"entities" : qUnion([Q0, Q1, Q2]), "endBound" : BoundingType.UP_TO_SURFACE, "depth" : 25 * mm, "endBoundEntityFace" : qUnion([Q3]), "offsetDistance" : 25 * mm});
        }
    });
